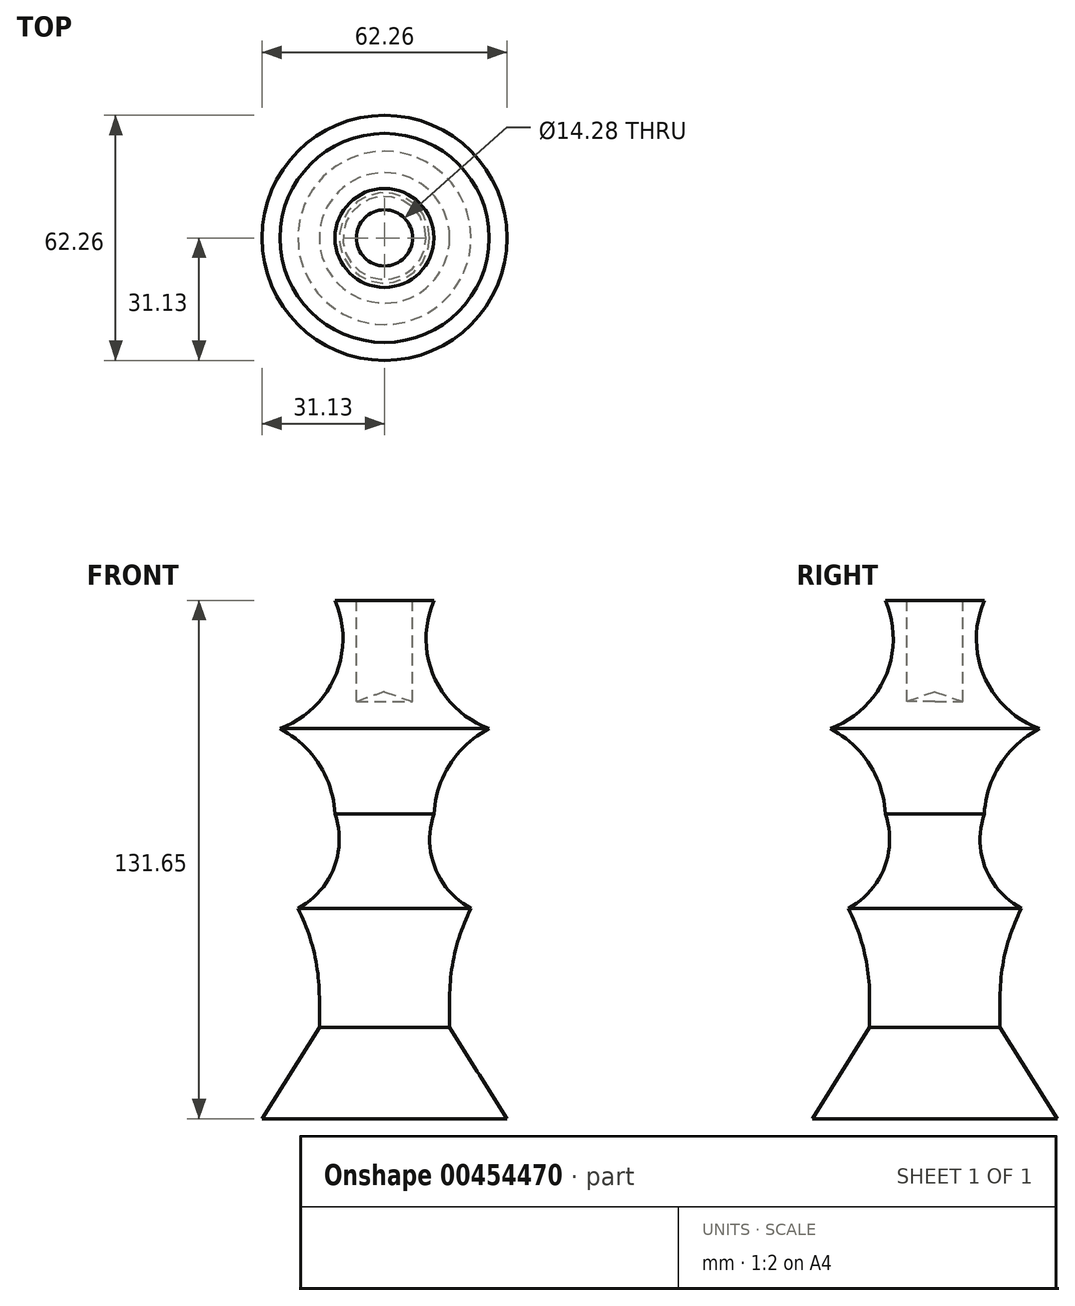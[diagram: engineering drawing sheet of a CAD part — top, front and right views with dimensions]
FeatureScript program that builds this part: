
annotation { "Feature Type Name" : "Feature", "Feature Type Description" : "" }
export const myFeature = defineFeature(function(context is Context, id is Id, definition is map)
    precondition{}
    {
        {
            var Q0;
            Q0=qCreatedBy(makeId("Front.planeOp"),FACE);
            var sketch = newSketch(context, id + "F0", { "sketchPlane" : qUnion([Q0])});
            skLineSegment(sketch, "E0", {"start": v(0, 58.83) * mm, "end": v(0, -63.97) * mm});
            skLineSegment(sketch, "E1", {"start": v(0, -63.97) * mm, "end": v(31.13, -63.97) * mm});
            skLineSegment(sketch, "E2", {"start": v(31.13, -63.97) * mm, "end": v(16.56, -40.84) * mm});
            skLineSegment(sketch, "E3", {"start": v(16.56, -40.84) * mm, "end": v(16.56, -33.13) * mm});
            skArc(sketch, "E4", {"start": v(21.99, -10.57) * mm, "mid": v(17.94, -21.52) * mm, "end": v(16.56, -33.13) * mm});
            skArc(sketch, "E5", {"start": v(12.57, 13.42) * mm, "mid": v(12.87, -0.3) * mm, "end": v(21.99, -10.57) * mm});
            skArc(sketch, "E6", {"start": v(26.56, 35.13) * mm, "mid": v(16.66, 26.14) * mm, "end": v(12.57, 13.42) * mm});
            skArc(sketch, "E7", {"start": v(12.57, 67.68) * mm, "mid": v(12.54, 48.38) * mm, "end": v(26.56, 35.13) * mm});
            skLineSegment(sketch, "E8", {"start": v(12.57, 67.68) * mm, "end": v(7.14, 67.68) * mm});
            skLineSegment(sketch, "E9", {"start": v(7.14, 67.68) * mm, "end": v(7.14, 41.98) * mm});
            skLineSegment(sketch, "E10", {"start": v(7.14, 41.98) * mm, "end": v(0, 44.5) * mm});
            skLineSegment(sketch, "E11", {"start": v(0, 44.5) * mm, "end": v(0, 37.98) * mm});
            skLineSegment(sketch, "E12", {"start": v(117.08, 94.24) * mm, "end": v(120.8, 91.95) * mm});
            skSolve(sketch);
        }
        {
            var Q0;
            {var subQ0=sQuery(id+"F0.wireOp",EDGE,"E1");Q0=makeQuery(id+"F0.imprint","IMPRINT",FACE,{"disambiguationData":[TD([[makeQuery(id+"F0.imprint","IMPRINT",EDGE,{"derivedFrom":subQ0}),1.0]])]});}
            var Q1;
            Q1=sQuery(id+"F0.wireOp",EDGE,"E0");
            revolve(context, id + "F1", {"entities" : qUnion([Q0]), "axis" : qUnion([Q1]), "revolveType" : RevolveType.FULL});
        }
    });
